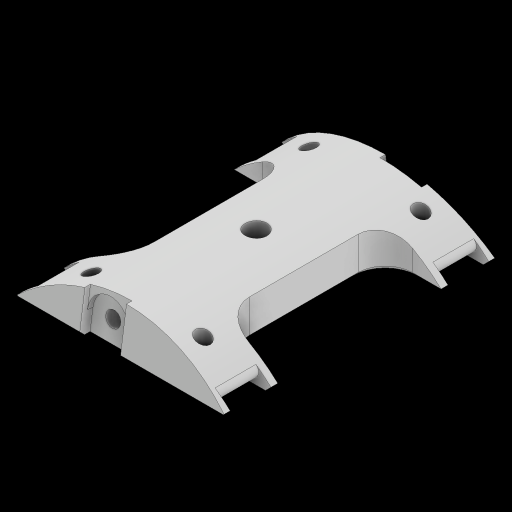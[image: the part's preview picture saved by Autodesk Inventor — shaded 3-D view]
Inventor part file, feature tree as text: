
AUTODESK INVENTOR PART (.ipt)
format: ipt  version: 2023 (Build 270158000, 158)  size: 339,968 bytes
history: native  units: mm
features: extrude x12, sketch x5, fillet x2, chamfer x1, plane x1, hole x1
ambient origin geometry x8: Origin, YZ Plane, XZ Plane, XY Plane, X Axis, Y Axis, Z Axis, Center Point
bodies: Solid1 (feature_tree)
feature tree (22):
  sketch  "Sketch1"  dims[d0=5.5mm d1=15.0mm d2=20.0mm]
  extrude  "Extrusion1"  Depth=20.0mm
  extrude  "Extrusion2"  Depth=17.0mm TaperAngle=0.0deg
  fillet  "Fillet2"  Radius=2.0mm
  chamfer  "Chamfer1"  Distance=200.0mm
  plane  "Work Plane1"
  extrude  "Extrusion3"  Depth=10.0mm
  extrude  "Extrusion4"  TaperAngle=90.0deg  [1 undecoded]
  extrude  "Extrusion5"  TaperAngle=90.0deg  [1 undecoded]
  extrude  "Extrusion6"  Depth=2.5mm
  sketch  "Sketch4"  dims[d18=100.0mm d20=90.0deg]
  extrude  "Extrusion10"  Depth=2.5mm
  extrude  "Extrusion11"  Depth=2.5mm
  extrude  "Extrusion12"  Depth=2.5mm TaperAngle=0.0deg
  sketch  "Sketch5"  dims[d21=260.34779mm d22=90.0deg d23=47.979859mm d24=10.93871mm d25=2.0mm d26=200.0mm d27=0.0mm d28=2.0mm d29=0.0mm d30=3.0mm d31=0.0mm d32=15.0mm d33=0.0mm d35=15.0mm d36=90.0deg d37=2.0mm d38=90.0deg d39=15.0mm d40=15.0mm d41=5.5mm d42=20.0mm d49=4.0mm d50=0.0mm d51=2.0mm d52=2.0mm d53=0.0mm d54=20.0mm d55=0.0mm d56=15.0mm d57=90.0deg d58=2.0mm d59=90.0deg d60=15.0mm d61=15.0mm d62=5.5mm d63=20.0mm d64=2.0mm d65=2.0mm d66=0.0mm d67=4.0mm d68=0.0mm d69=20.0mm d70=0.0mm d72=8.0mm d73=6.0mm d74=20.0mm d75=2.0mm d76=90.0deg d77=20.0mm d78=0.0mm d79=2.5mm d8=0.872665mm d17=0.0mm d19=0.0mm d71=0.0mm d80=0.0mm d81=0.0mm d82=0.0mm]
  extrude  "Extrusion13"  Depth=2.5mm TaperAngle=0.0deg
  extrude  "Extrusion14"  Depth=2.5mm TaperAngle=0.0deg
  extrude  "Extrusion15"  Depth=2.5mm TaperAngle=0.0deg
  hole  "Hole1"  [1 undecoded]
  fillet  "Fillet4"  [1 undecoded]
  sketch  "Sketch2"  dims[d4=35.0mm d5=17.0mm d6=0.0mm d7=2.0mm d10=200.0mm d11=0.0mm]
  sketch  "Sketch3"  dims[d13=10.0mm d14=2.0mm d15=4.0mm d16=13.962634mm]
note: 4 required parameter values undecoded (feature->parameter linkage not recoverable at this tier; creation-order binding heuristic only, values carry confidence <= 0.55)
